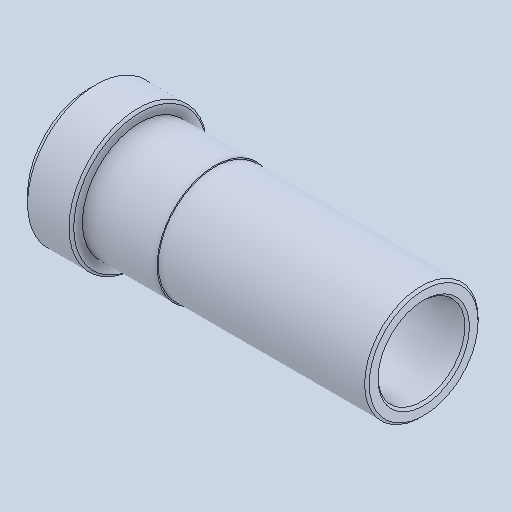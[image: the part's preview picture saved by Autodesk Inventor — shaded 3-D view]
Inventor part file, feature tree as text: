
AUTODESK INVENTOR PART (.ipt)
format: ipt  version: 2024.2 (Build 282272000, 272)  size: 145,408 bytes
history: native  units: in
note: dims shown in document units (in); Inventor stores cm internally (conversion verified against a paired STEP export)
features: chamfer x1
ambient origin geometry x8: Origin, YZ Plane, XZ Plane, XY Plane, X Axis, Y Axis, Z Axis, Center Point
bodies: Solid1 (feature_tree)
feature tree (1):
  chamfer  "Chamfer3"  [1 undecoded]
note: 1 required parameter value undecoded (feature->parameter linkage not recoverable at this tier; creation-order binding heuristic only, values carry confidence <= 0.55)
